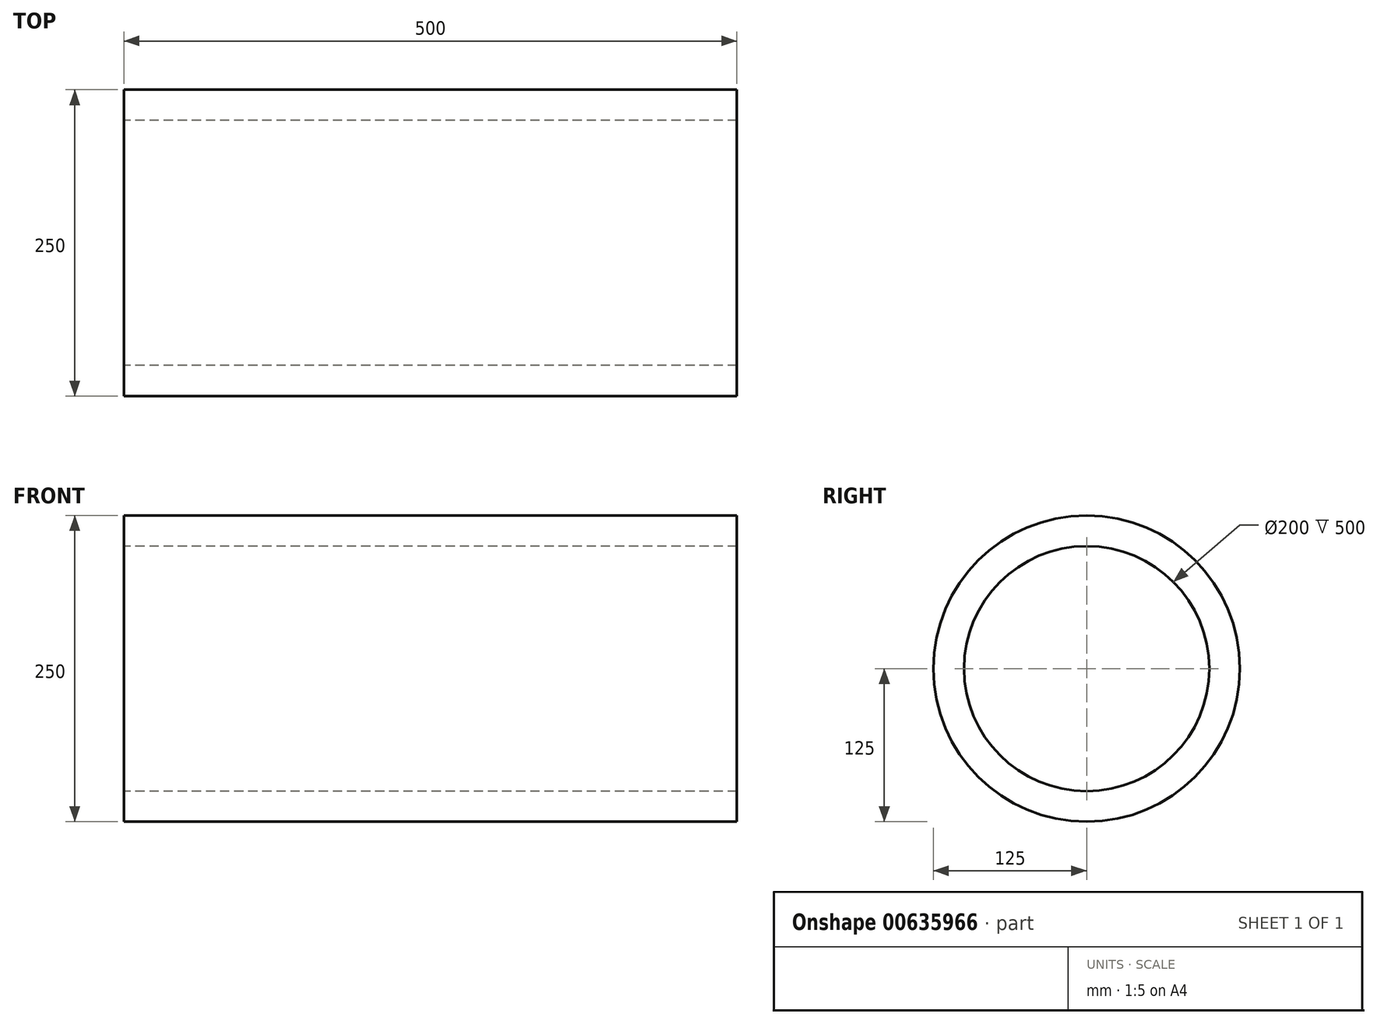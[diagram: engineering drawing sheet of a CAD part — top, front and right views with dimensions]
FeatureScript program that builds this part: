
annotation { "Feature Type Name" : "Feature", "Feature Type Description" : "" }
export const myFeature = defineFeature(function(context is Context, id is Id, definition is map)
    precondition{}
    {
        {
            var Q0;
            Q0=qCreatedBy(makeId("Right.planeOp"),FACE);
            var sketch = newSketch(context, id + "F0", { "sketchPlane" : qUnion([Q0])});
            skCircle(sketch, "E0", {"center": v(0, 0) * mm, "radius": 125 * mm});
            skCircle(sketch, "E1", {"center": v(0, 0) * mm, "radius": 100 * mm});
            skSolve(sketch);
        }
        {
            var Q0;
            Q0=makeQuery(id+"F0.imprint","IMPRINT",FACE,{"disambiguationData":[TD([[makeQuery(id+"F0.imprint","IMPRINT",EDGE,{"derivedFrom":sQuery(id+"F0.wireOp",EDGE,"E0")}),1.0]])]});
            extrude(context, id + "F1", {"entities" : qUnion([Q0]), "depth" : 500 * mm, "offsetDistance" : 25 * mm});
        }
    });
